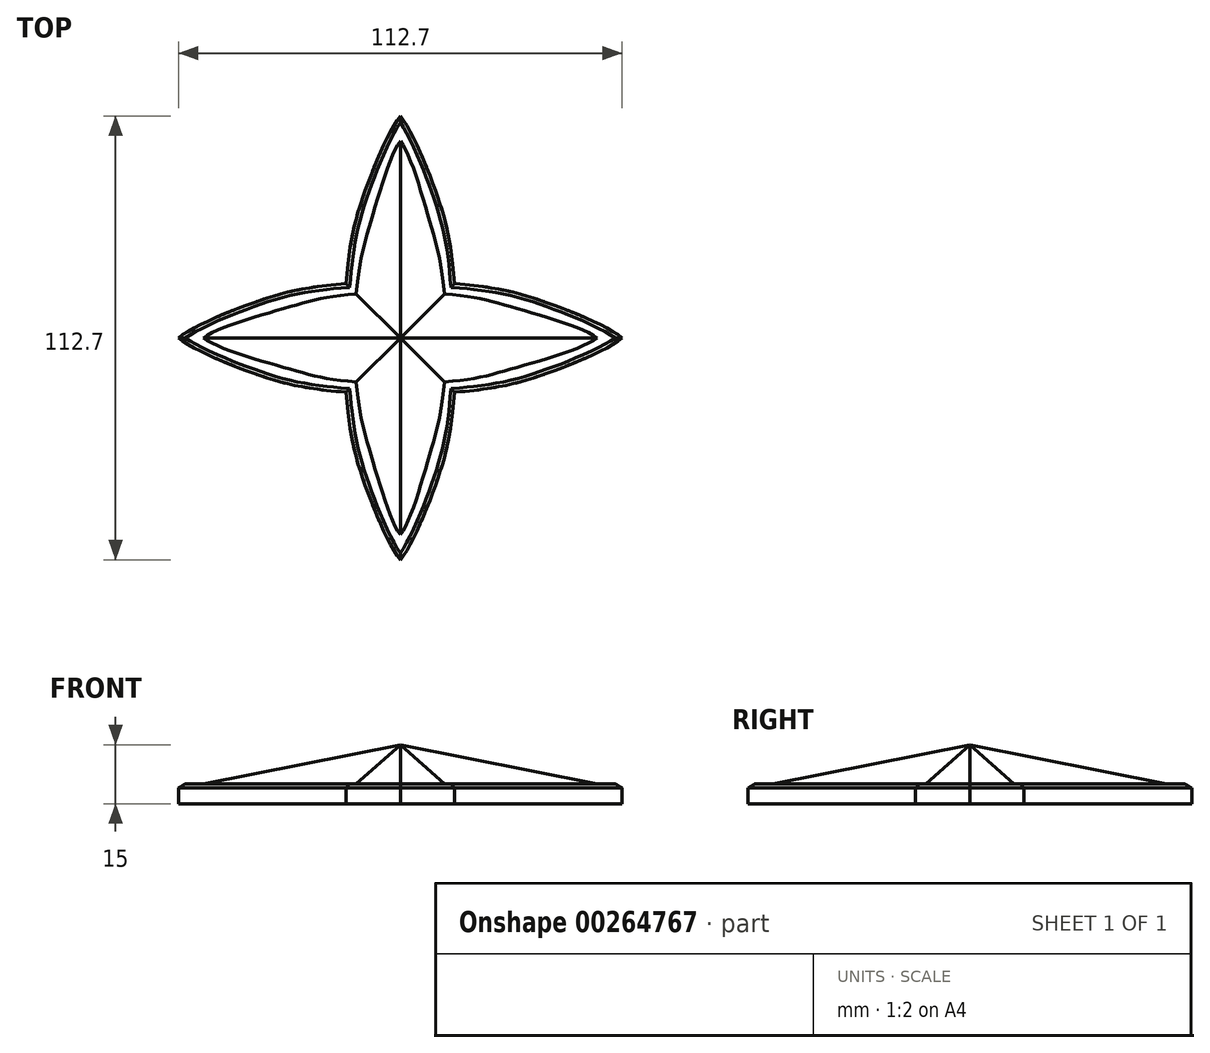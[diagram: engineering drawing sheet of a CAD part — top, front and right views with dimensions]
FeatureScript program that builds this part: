
annotation { "Feature Type Name" : "Feature", "Feature Type Description" : "" }
export const myFeature = defineFeature(function(context is Context, id is Id, definition is map)
    precondition{}
    {
        {
            var Q0;
            Q0=qCreatedBy(makeId("Top.planeOp"),FACE);
            var sketch = newSketch(context, id + "F0", { "sketchPlane" : qUnion([Q0])});
            skLineSegment(sketch, "E0", {"start": v(0, 0) * mm, "end": v(0, 50) * mm});
            skLineSegment(sketch, "E1", {"start": v(0, 0) * mm, "end": v(-50, 0) * mm});
            skFitSpline(sketch, "E2", {"points": [v(0, 50) * mm, v(-50, 0) * mm], "startDerivative": vector(-22.26, -93.04) * mm, "endDerivative": vector(-77.74, -6.96) * mm});
            skFitSpline(sketch, "E3.MirrorCS", {"points": [v(0, 50) * mm, v(50, 0) * mm], "startDerivative": vector(22.26, -93.04) * mm, "endDerivative": vector(77.74, -6.96) * mm});
            skFitSpline(sketch, "E4.MirrorCS", {"points": [v(0, -50) * mm, v(-50, 0) * mm], "startDerivative": vector(-22.26, 93.04) * mm, "endDerivative": vector(-77.74, 6.96) * mm});
            skFitSpline(sketch, "E5.MirrorCS", {"points": [v(0, -50) * mm, v(50, 0) * mm], "startDerivative": vector(22.26, 93.04) * mm, "endDerivative": vector(77.74, 6.96) * mm});
            skSolve(sketch);
        }
        {
            var Q0;
            Q0=qCreatedBy(makeId("Top.planeOp"),FACE);
            var sketch = newSketch(context, id + "F1", { "sketchPlane" : qUnion([Q0])});
            skFitSpline(sketch, "E6", {"points": [v(0, 49.98) * mm, v(-7.34, 30.13) * mm, v(-11.2, 11.2) * mm], "startDerivative": vector(-14.95, -18.4) * mm, "endDerivative": vector(-4.03, -50.51) * mm});
            skFitSpline(sketch, "E7.MirrorCS", {"points": [v(0, 49.98) * mm, v(7.34, 30.13) * mm, v(11.2, 11.2) * mm], "startDerivative": vector(14.95, -18.4) * mm, "endDerivative": vector(4.03, -50.51) * mm});
            skFitSpline(sketch, "E8.MirrorCS", {"points": [v(0, -49.98) * mm, v(-7.34, -30.13) * mm, v(-11.2, -11.2) * mm], "startDerivative": vector(-14.95, 18.4) * mm, "endDerivative": vector(-4.03, 50.51) * mm});
            skFitSpline(sketch, "E9.MirrorCS", {"points": [v(0, -49.98) * mm, v(7.34, -30.13) * mm, v(11.2, -11.2) * mm], "startDerivative": vector(14.95, 18.4) * mm, "endDerivative": vector(4.03, 50.51) * mm});
            skLineSegment(sketch, "E10", {"start": v(-11.2, 11.2) * mm, "end": v(11.2, -11.2) * mm, "construction": true});
            skLineSegment(sketch, "E11", {"start": v(11.2, 11.2) * mm, "end": v(-11.2, -11.2) * mm, "construction": true});
            skFitSpline(sketch, "E12.MirrorCS", {"points": [v(-49.98, 0) * mm, v(-30.13, -7.34) * mm, v(-11.2, -11.2) * mm], "startDerivative": vector(18.4, -14.95) * mm, "endDerivative": vector(50.51, -4.03) * mm});
            skFitSpline(sketch, "E13.MirrorCS", {"points": [v(-49.98, 0) * mm, v(-30.13, 7.34) * mm, v(-11.2, 11.2) * mm], "startDerivative": vector(18.4, 14.95) * mm, "endDerivative": vector(50.51, 4.03) * mm});
            skFitSpline(sketch, "E14.MirrorCS", {"points": [v(49.98, 0) * mm, v(30.13, 7.34) * mm, v(11.2, 11.2) * mm], "startDerivative": vector(-18.4, 14.95) * mm, "endDerivative": vector(-50.51, 4.03) * mm});
            skFitSpline(sketch, "E15.MirrorCS", {"points": [v(49.98, 0) * mm, v(30.13, -7.34) * mm, v(11.2, -11.2) * mm], "startDerivative": vector(-18.4, -14.95) * mm, "endDerivative": vector(-50.51, -4.03) * mm});
            skLineSegment(sketch, "E16", {"start": v(0, 49.98) * mm, "end": v(0, 0) * mm, "construction": true});
            skLineSegment(sketch, "E17", {"start": v(0, 0) * mm, "end": v(0, -49.98) * mm, "construction": true});
            skLineSegment(sketch, "E18", {"start": v(0, 0) * mm, "end": v(49.98, 0) * mm, "construction": true});
            skLineSegment(sketch, "E19", {"start": v(0, 0) * mm, "end": v(-49.98, 0) * mm, "construction": true});
            skSolve(sketch);
        }
        {
            var Q0;
            Q0=qCreatedBy(makeId("Top.planeOp"),FACE);
            var sketch = newSketch(context, id + "F2", { "sketchPlane" : qUnion([Q0])});
            skFitSpline(sketch, "E20", {"points": [v(0, 56.35) * mm, v(-9.04, 37.09) * mm, v(-13.78, 13.78) * mm], "startDerivative": vector(-18.4, -22.65) * mm, "endDerivative": vector(-4.96, -62.19) * mm});
            skFitSpline(sketch, "E21.MirrorCS", {"points": [v(0, 56.35) * mm, v(9.04, 37.09) * mm, v(13.78, 13.78) * mm], "startDerivative": vector(18.4, -22.65) * mm, "endDerivative": vector(4.96, -62.19) * mm});
            skFitSpline(sketch, "E22.MirrorCS", {"points": [v(0, -56.35) * mm, v(-9.04, -37.09) * mm, v(-13.78, -13.78) * mm], "startDerivative": vector(-18.4, 22.65) * mm, "endDerivative": vector(-4.96, 62.19) * mm});
            skFitSpline(sketch, "E23.MirrorCS", {"points": [v(0, -56.35) * mm, v(9.04, -37.09) * mm, v(13.78, -13.78) * mm], "startDerivative": vector(18.4, 22.65) * mm, "endDerivative": vector(4.96, 62.19) * mm});
            skLineSegment(sketch, "E24", {"start": v(-13.78, 13.78) * mm, "end": v(13.78, -13.78) * mm});
            skLineSegment(sketch, "E25", {"start": v(13.78, 13.78) * mm, "end": v(-13.78, -13.78) * mm});
            skFitSpline(sketch, "E26.MirrorCS", {"points": [v(-56.35, 0) * mm, v(-37.09, -9.04) * mm, v(-13.78, -13.78) * mm], "startDerivative": vector(22.65, -18.4) * mm, "endDerivative": vector(62.19, -4.96) * mm});
            skFitSpline(sketch, "E27.MirrorCS", {"points": [v(-56.35, 0) * mm, v(-37.09, 9.04) * mm, v(-13.78, 13.78) * mm], "startDerivative": vector(22.65, 18.4) * mm, "endDerivative": vector(62.19, 4.96) * mm});
            skFitSpline(sketch, "E28.MirrorCS", {"points": [v(56.35, 0) * mm, v(37.09, 9.04) * mm, v(13.78, 13.78) * mm], "startDerivative": vector(-22.65, 18.4) * mm, "endDerivative": vector(-62.19, 4.96) * mm});
            skFitSpline(sketch, "E29.MirrorCS", {"points": [v(56.35, 0) * mm, v(37.09, -9.04) * mm, v(13.78, -13.78) * mm], "startDerivative": vector(-22.65, -18.4) * mm, "endDerivative": vector(-62.19, -4.96) * mm});
            skLineSegment(sketch, "E30", {"start": v(-56.35, 0) * mm, "end": v(0, 0) * mm, "construction": true});
            skLineSegment(sketch, "E31", {"start": v(0, 0) * mm, "end": v(56.35, 0) * mm, "construction": true});
            skLineSegment(sketch, "E32", {"start": v(0, 0) * mm, "end": v(0, 56.35) * mm, "construction": true});
            skLineSegment(sketch, "E33", {"start": v(0, 0) * mm, "end": v(0, -56.35) * mm, "construction": true});
            skSolve(sketch);
        }
        {
            var Q0;
            Q0=qCreatedBy(makeId("Top.planeOp"),FACE);
            cPlane(context, id + "F3", {"entities" : qUnion([Q0]), "cplaneType" : CPlaneType.OFFSET, "offset" : 10 * mm, "width" : 150 * mm, "height" : 150 * mm});
        }
        {
            var Q0;
            Q0=qCreatedBy(id+"F3.planeOp",FACE);
            var sketch = newSketch(context, id + "F4", { "sketchPlane" : qUnion([Q0])});
            skPoint(sketch, "E34", {"position": v(0, 0) * mm});
            skSolve(sketch);
        }
        {
            var Q0;
            Q0=makeQuery(id+"F1.imprint","IMPRINT",FACE,{"disambiguationData":[TD([[makeQuery(id+"F1.imprint","IMPRINT",EDGE,{"derivedFrom":sQuery(id+"F1.wireOp",EDGE,"E6")}),1.0]])]});
            var Q1;
            Q1=sQuery(id+"F4.wireOp",VERTEX,"E34");
            loft(context, id + "F5", {"sheetProfilesArray" : [{ "sheetProfileEntities" : qUnion([Q0]) }, { "sheetProfileEntities" : qUnion([Q1]) }]});
        }
        {
            var Q0;
            {var subQ0=sQuery(id+"F2.wireOp",EDGE,"E20");Q0=makeQuery(id+"F2.imprint","IMPRINT",FACE,{"disambiguationData":[TD([[makeQuery(id+"F2.imprint","IMPRINT",EDGE,{"derivedFrom":subQ0}),1.0]])]});}
            var Q1;
            {var subQ4=sQuery(id+"F2.wireOp",EDGE,"E26.MirrorCS");Q1=makeQuery(id+"F2.imprint","IMPRINT",FACE,{"disambiguationData":[TD([[makeQuery(id+"F2.imprint","IMPRINT",EDGE,{"derivedFrom":subQ4}),1.0]])]});}
            var Q2;
            {var subQ0=sQuery(id+"F2.wireOp",EDGE,"E22.MirrorCS");Q2=makeQuery(id+"F2.imprint","IMPRINT",FACE,{"disambiguationData":[TD([[makeQuery(id+"F2.imprint","IMPRINT",EDGE,{"derivedFrom":subQ0}),-1.0]])]});}
            var Q3;
            {var subQ4=sQuery(id+"F2.wireOp",EDGE,"E28.MirrorCS");Q3=makeQuery(id+"F2.imprint","IMPRINT",FACE,{"disambiguationData":[TD([[makeQuery(id+"F2.imprint","IMPRINT",EDGE,{"derivedFrom":subQ4}),1.0]])]});}
            extrude(context, id + "F6", {"entities" : qUnion([Q0, Q1, Q2, Q3]), "operationType" : NewBodyOperationType.ADD, "oppositeDirection" : true, "depth" : 5 * mm, "offsetDistance" : 25 * mm});
        }
        {
            var Q0;
            Q0=makeQuery(id+"F6.opExtrude","CAP_EDGE",EDGE,{"disambiguationData":[OSD([sQuery(id+"F2.wireOp",EDGE,"E26.MirrorCS")])],"isStart":true});
            var Q1;
            Q1=makeQuery(id+"F6.opExtrude","CAP_EDGE",EDGE,{"disambiguationData":[OSD([sQuery(id+"F2.wireOp",EDGE,"E27.MirrorCS")])],"isStart":true});
            var Q2;
            Q2=makeQuery(id+"F6.opExtrude","CAP_EDGE",EDGE,{"disambiguationData":[OSD([sQuery(id+"F2.wireOp",EDGE,"E20")])],"isStart":true});
            var Q3;
            Q3=makeQuery(id+"F6.opExtrude","CAP_EDGE",EDGE,{"disambiguationData":[OSD([sQuery(id+"F2.wireOp",EDGE,"E21.MirrorCS")])],"isStart":true});
            var Q4;
            Q4=makeQuery(id+"F6.opExtrude","CAP_EDGE",EDGE,{"disambiguationData":[OSD([sQuery(id+"F2.wireOp",EDGE,"E28.MirrorCS")])],"isStart":true});
            var Q5;
            Q5=makeQuery(id+"F6.opExtrude","CAP_EDGE",EDGE,{"disambiguationData":[OSD([sQuery(id+"F2.wireOp",EDGE,"E29.MirrorCS")])],"isStart":true});
            var Q6;
            Q6=makeQuery(id+"F6.opExtrude","CAP_EDGE",EDGE,{"disambiguationData":[OSD([sQuery(id+"F2.wireOp",EDGE,"E23.MirrorCS")])],"isStart":true});
            var Q7;
            Q7=makeQuery(id+"F6.opExtrude","CAP_EDGE",EDGE,{"disambiguationData":[OSD([sQuery(id+"F2.wireOp",EDGE,"E22.MirrorCS")])],"isStart":true});
            chamfer(context, id + "F7", {"entities" : qUnion([Q0, Q1, Q2, Q3, Q4, Q5, Q6, Q7]), "width" : 1 * mm, "tangentPropagation" : true});
        }
    });
